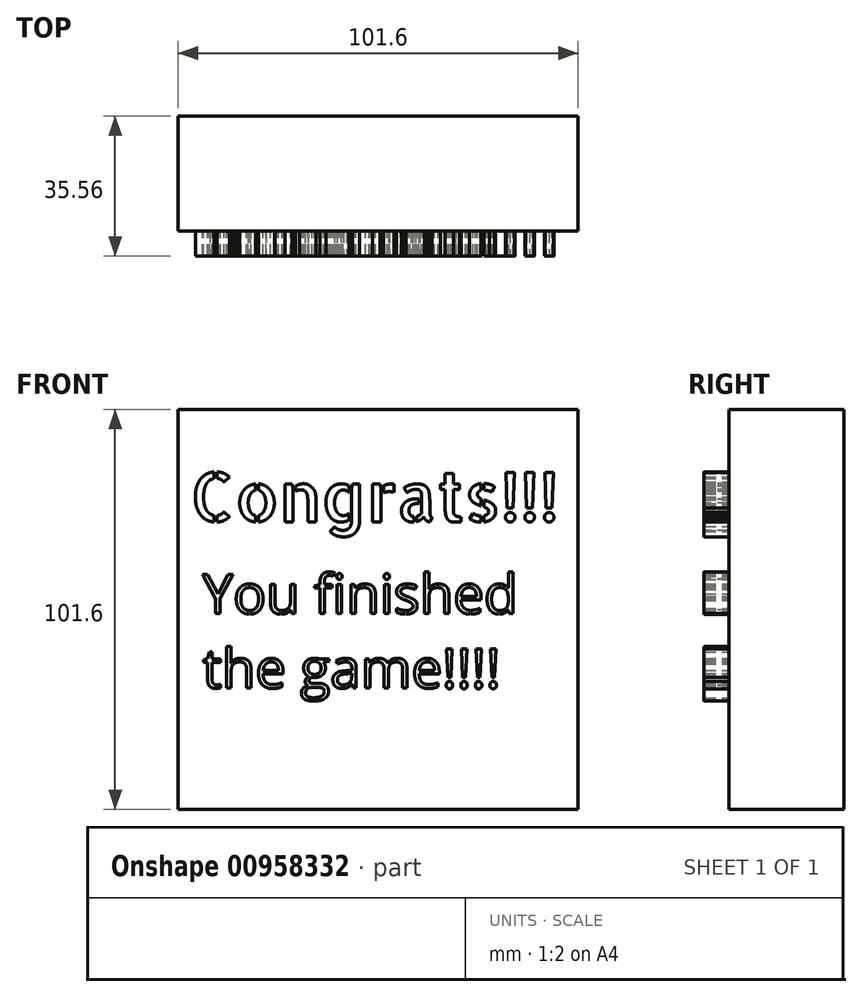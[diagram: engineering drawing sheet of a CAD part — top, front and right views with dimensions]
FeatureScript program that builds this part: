
annotation { "Feature Type Name" : "Feature", "Feature Type Description" : "" }
export const myFeature = defineFeature(function(context is Context, id is Id, definition is map)
    precondition{}
    {
        {
            var Q0;
            Q0=qCreatedBy(makeId("Front.planeOp"),FACE);
            var sketch = newSketch(context, id + "F0", { "sketchPlane" : qUnion([Q0])});
            skLineSegment(sketch, "E0", {"start": v(-38.78, -22.52) * mm, "end": v(61.31, -22.52) * mm});
            skLineSegment(sketch, "E1", {"start": v(61.31, -22.52) * mm, "end": v(61.31, 79.08) * mm});
            skLineSegment(sketch, "E2", {"start": v(61.31, 79.08) * mm, "end": v(-40.29, 79.08) * mm});
            skLineSegment(sketch, "E3", {"start": v(-40.29, 79.08) * mm, "end": v(-40.29, -22.52) * mm});
            skLineSegment(sketch, "E4", {"start": v(-40.29, -22.52) * mm, "end": v(-38.78, -22.52) * mm});
            skSolve(sketch);
        }
        {
            var Q0;
            Q0=makeQuery(id+"F0.imprint","IMPRINT",FACE,{"disambiguationData":[TD([[makeQuery(id+"F0.imprint","IMPRINT",EDGE,{"derivedFrom":sQuery(id+"F0.wireOp",EDGE,"E0")}),1.0]])]});
            extrude(context, id + "F1", {"entities" : qUnion([Q0]), "oppositeDirection" : true, "depth" : 29.2 * mm, "offsetDistance" : 25.4 * mm});
        }
        {
            var Q0;
            Q0=makeQuery(id+"F1.opExtrude","CAP_FACE",FACE,{"disambiguationData":[OSD([sQuery(id+"F0.wireOp",EDGE,"E0"),sQuery(id+"F0.wireOp",EDGE,"E1"),sQuery(id+"F0.wireOp",EDGE,"E2"),sQuery(id+"F0.wireOp",EDGE,"E3"),sQuery(id+"F0.wireOp",EDGE,"E4")])],"isStart":true});
            var sketch = newSketch(context, id + "F2", { "sketchPlane" : qUnion([Q0])});
            skText(sketch, "E5", { "text": "Congrats!!!", "fontName": "AllertaStencil-Regular.ttf"});
            skText(sketch, "E6", { "text": "You finished\nthe game!!!!\n\n", "fontName": "OpenSans-Regular.ttf"});
            const initialGuessF2  = {"E5": [-0.03726, 0.05057, 1, 0, 0.0125], "E6": [-0.0341, 0.02722, 1, 0, 0.01]};
            skSetInitialGuess(sketch, initialGuessF2);
            skSolve(sketch);
        }
        {
            var Q0;
            Q0 = qSketchRegion(id + "F2", true);
            extrude(context, id + "F3", {"entities" : qUnion([Q0]), "operationType" : NewBodyOperationType.ADD, "depth" : 6.35 * mm, "offsetDistance" : 25.4 * mm});
        }
    });
